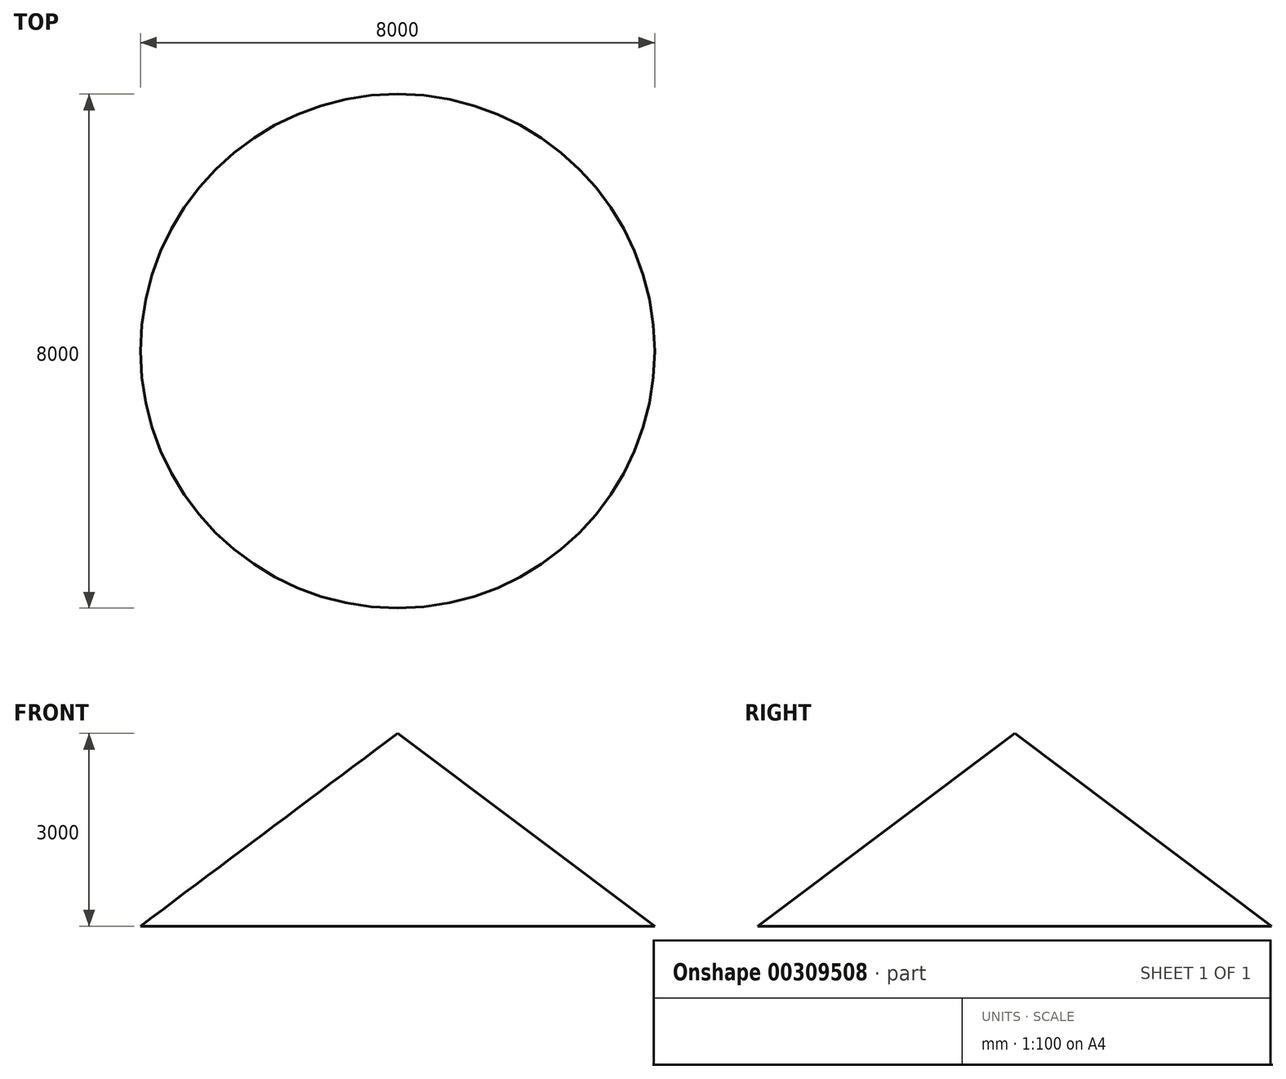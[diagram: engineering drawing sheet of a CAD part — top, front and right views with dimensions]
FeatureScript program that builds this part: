
annotation { "Feature Type Name" : "Feature", "Feature Type Description" : "" }
export const myFeature = defineFeature(function(context is Context, id is Id, definition is map)
    precondition{}
    {
        {
            var Q0;
            Q0=qCreatedBy(makeId("Front.planeOp"),FACE);
            var sketch = newSketch(context, id + "F0", { "sketchPlane" : qUnion([Q0])});
            skLineSegment(sketch, "E0", {"start": v(0, -797.27) * mm, "end": v(4000, -797.27) * mm});
            skLineSegment(sketch, "E1", {"start": v(4000, -797.27) * mm, "end": v(0, 2202.73) * mm});
            skLineSegment(sketch, "E2", {"start": v(0, 2202.73) * mm, "end": v(0, -797.27) * mm});
            skSolve(sketch);
        }
        {
            var Q0;
            Q0=qCreatedBy(makeId("Front.planeOp"),FACE);
            var sketch = newSketch(context, id + "F1", { "sketchPlane" : qUnion([Q0])});
            skLineSegment(sketch, "E3", {"start": v(0, 3321.43) * mm, "end": v(0, -2678.57) * mm, "construction": true});
            skSolve(sketch);
        }
        {
            var Q0;
            Q0=makeQuery(id+"F0.imprint","IMPRINT",FACE,{"disambiguationData":[TD([[makeQuery(id+"F0.imprint","IMPRINT",EDGE,{"derivedFrom":sQuery(id+"F0.wireOp",EDGE,"E0")}),1.0]])]});
            var Q1;
            Q1=sQuery(id+"F1.wireOp",EDGE,"E3");
            revolve(context, id + "F2", {"entities" : qUnion([Q0]), "axis" : qUnion([Q1]), "revolveType" : RevolveType.FULL});
        }
    });
